# Revit family: 0048210
name_source: partatom
category: Lighting Fixtures
revit_build: Autodesk Revit 2017 (Build: 20190507_1515(x64)
units: mm (PartAtom-declared; Revit-internal decimal feet)

## family parameters
Cut with Voids When Loaded = No
Host = Face
Light Source = No
OmniClass Number = 23.80.70.00
OmniClass Title = Lighting
Part Type = Normal
Room Calculation Point = No
Round Connector Dimension = Use Diameter
Shared = No

## types (1)
- 0048210 Start Flood IP66 21000lm 740 WB
    100W_SYL = No
    150W_SYL = Yes
    200W_SYL = No
    50W_SYL = No
    Apparent Load = 150 VA
    Assembly Code = D5020200
    AssetType = Fixed
    AxisDepth_SYL = 72 mm
    AxisHeight_SYL = 100 mm  [stored 0.328084 ft]
    AxisOffsetWingEnd_SYL = 20 mm  [stored 0.0656168 ft]
    ClassificationName = Uniclass2015
    ClassificationValue = EF_70_80
    Cost = 0 $
    Default Elevation = 1219 mm
    DocumentationLiterature = http://www.sylvania-lighting.com
    ElectricShockClassification = Class I
    IfcExportAs = IfcLightFixtureType
    IfcExportType = IfcLightFixtureType
    ImpactProtectionIndex = IK08
    IngressProtection = IP66
    Keynote = 16500
    Lamp = LED
    LampColourRenderingIndex = 70
    LampColourTemperature = 4000 K
    LampNominalLuminous = 21686 lm
    LampsType = LED
    LengthIn_SYL = 295 mm  [stored 0.967848 ft]
    LuminousEfficacy = 144.6 lm/W
    Manufacturer = Feilo Sylvania
    ManufacturerName = Feilo Sylvania
    Material_1_SYL = Steel, Paint Finish, Dark Gray, Matte
    Material_2_SYL = <By Category>
    Material_3_SYL = <By Category>
    Material_4_SYL = <By Category>
    Model = Start Flood IP66 21000lm 740 WB
    ModelNumber = 0048210
    ModelReference = Start Flood IP66 21000lm 740 WB
    Name = Start Flood IP66 21000lm 740 WB
    NominalDepth = 77 mm
    NominalHeight = 330 mm
    NominalLength = 451 mm
    PowerConsumption = 149 W
    PowerFactor = 0.99
    RadiusInBracket_SYL = 2 mm  [stored 0.00656168 ft]
    RadiusOutBracket_SYL = 5 mm  [stored 0.0164042 ft]
    ThicknessBracket_SYL = 3 mm  [stored 0.00984252 ft]
    Type Image = <None>
    TypeHead_SYL = START Flood IP66 150W luminaire : 0048210 Start Flood IP66 21000lm 740 WB
    TypeName = Start Flood IP66 21000lm 740 WB
    URL = http://www.sylvania-lighting.com
    Voltage = 230 V
    Weight = 4.6 kg
    WidthBracket_SYL = 40 mm  [stored 0.131234 ft]
    WingLength_SYL = 142 mm  [stored 0.465879 ft]
    WingRadius_SYL = 10 mm  [stored 0.0328084 ft]

note: [stored X ft] marks values corroborated as IEEE doubles in the binary element streams (Revit-internal decimal feet)

## geometry (parser evidence)
native form markers: Sweep x5
no freeform markers — native parametric forms only
